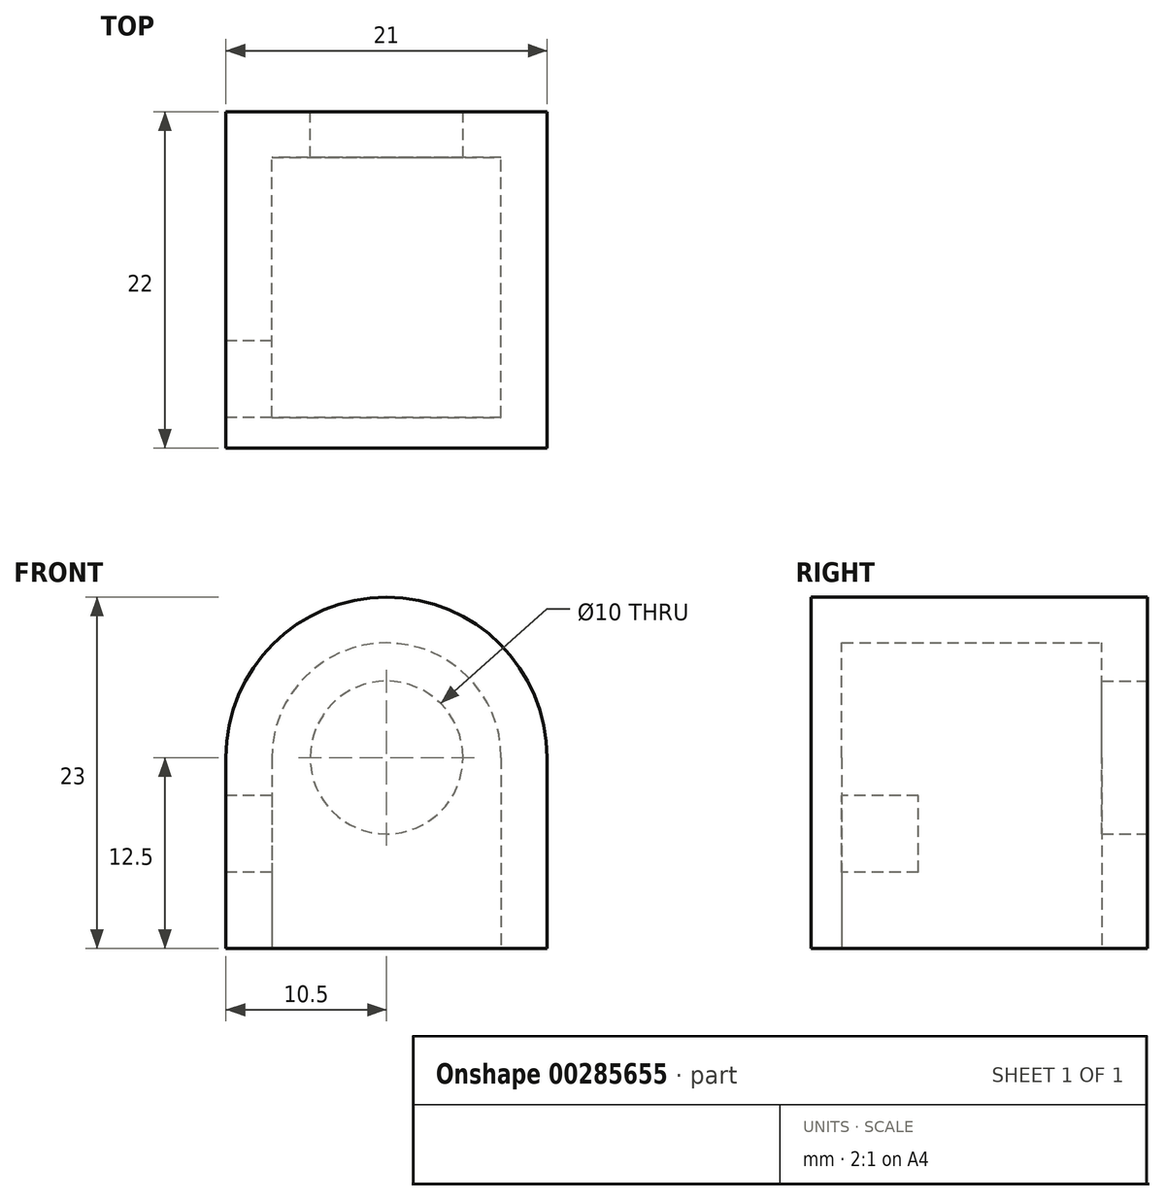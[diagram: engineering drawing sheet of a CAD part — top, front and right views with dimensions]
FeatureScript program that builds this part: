
annotation { "Feature Type Name" : "Feature", "Feature Type Description" : "" }
export const myFeature = defineFeature(function(context is Context, id is Id, definition is map)
    precondition{}
    {
        {
            var Q0;
            Q0=qCreatedBy(makeId("Front.planeOp"),FACE);
            var sketch = newSketch(context, id + "F0", { "sketchPlane" : qUnion([Q0])});
            skCircle(sketch, "E0", {"center": v(0, 0) * mm, "radius": 5 * mm});
            skArc(sketch, "E1", {"start": v(7.5, 0) * mm, "mid": v(0, 7.5) * mm, "end": v(-7.5, 0) * mm});
            skLineSegment(sketch, "E2.top", {"start": v(-7.5, -12.5) * mm, "end": v(7.5, -12.5) * mm});
            skLineSegment(sketch, "E2.left", {"start": v(-7.5, 0) * mm, "end": v(-7.5, -12.5) * mm});
            skLineSegment(sketch, "E2.right", {"start": v(7.5, 0) * mm, "end": v(7.5, -12.5) * mm});
            skSolve(sketch);
        }
        {
            var Q0;
            Q0=makeQuery(id+"F0.imprint","IMPRINT",FACE,{"disambiguationData":[TD([[makeQuery(id+"F0.imprint","IMPRINT",EDGE,{"derivedFrom":sQuery(id+"F0.wireOp",EDGE,"E0")}),-1.0]])]});
            extrude(context, id + "F1", {"entities" : qUnion([Q0]), "depth" : 3 * mm});
        }
        {
            var Q0;
            Q0=qCreatedBy(makeId("Front.planeOp"),FACE);
            var sketch = newSketch(context, id + "F2", { "sketchPlane" : qUnion([Q0])});
            skArc(sketch, "E3", {"start": v(10.5, 0) * mm, "mid": v(0, 10.5) * mm, "end": v(-10.5, 0) * mm});
            skLineSegment(sketch, "E4.top", {"start": v(-10.5, -12.5) * mm, "end": v(-7.5, -12.5) * mm});
            skLineSegment(sketch, "E4.left", {"start": v(-10.5, 0) * mm, "end": v(-10.5, -12.5) * mm});
            skLineSegment(sketch, "E4.right", {"start": v(10.5, 0) * mm, "end": v(10.5, -12.5) * mm});
            skArc(sketch, "E5", {"start": v(7.5, 0) * mm, "mid": v(0, 7.5) * mm, "end": v(-7.5, 0) * mm});
            skLineSegment(sketch, "E6", {"start": v(-7.5, 0) * mm, "end": v(-7.5, -12.5) * mm});
            skLineSegment(sketch, "E7", {"start": v(7.5, 0) * mm, "end": v(7.5, -12.5) * mm});
            skLineSegment(sketch, "E8", {"start": v(7.5, -12.5) * mm, "end": v(10.5, -12.5) * mm});
            skSolve(sketch);
        }
        {
            var Q0;
            Q0=makeQuery(id+"F2.imprint","IMPRINT",FACE,{"disambiguationData":[TD([[makeQuery(id+"F2.imprint","IMPRINT",EDGE,{"derivedFrom":sQuery(id+"F2.wireOp",EDGE,"E3")}),1.0]])]});
            extrude(context, id + "F3", {"entities" : qUnion([Q0]), "operationType" : NewBodyOperationType.ADD, "depth" : 20 * mm});
        }
        {
            var Q0;
            Q0=makeQuery(id+"F3.opExtrude","CAP_FACE",FACE,{"disambiguationData":[OSD([sQuery(id+"F2.wireOp",EDGE,"E3"),sQuery(id+"F2.wireOp",EDGE,"E4.top"),sQuery(id+"F2.wireOp",EDGE,"E4.left"),sQuery(id+"F2.wireOp",EDGE,"E4.right"),sQuery(id+"F2.wireOp",EDGE,"E5"),sQuery(id+"F2.wireOp",EDGE,"E6"),sQuery(id+"F2.wireOp",EDGE,"E7"),sQuery(id+"F2.wireOp",EDGE,"E8")])],"isStart":false});
            var sketch = newSketch(context, id + "F4", { "sketchPlane" : qUnion([Q0])});
            skArc(sketch, "E9", {"start": v(10.5, 0) * mm, "mid": v(0, 10.5) * mm, "end": v(-10.5, 0) * mm});
            skLineSegment(sketch, "E10", {"start": v(-10.5, 0) * mm, "end": v(-10.5, -12.5) * mm});
            skLineSegment(sketch, "E11", {"start": v(-10.5, -12.5) * mm, "end": v(10.5, -12.5) * mm});
            skLineSegment(sketch, "E12", {"start": v(10.5, -12.5) * mm, "end": v(10.5, 0) * mm});
            skSolve(sketch);
        }
        {
            var Q0;
            Q0=qSketchRegion(id+"F4",true);
            extrude(context, id + "F5", {"entities" : qUnion([Q0]), "operationType" : NewBodyOperationType.ADD, "depth" : 2 * mm});
        }
        {
            var Q0;
            Q0=makeQuery(id+"F5.boolean.opBoolean","MERGE",FACE,{"derivedFrom":[makeQuery(id+"F3.opExtrude","SWEPT_FACE",FACE,{"disambiguationData":[OSD([sQuery(id+"F2.wireOp",EDGE,"E4.left")])]}),makeQuery(id+"F5.opExtrude","SWEPT_FACE",FACE,{"disambiguationData":[OSD([sQuery(id+"F4.wireOp",EDGE,"E10")])]})]});
            var sketch = newSketch(context, id + "F6", { "sketchPlane" : qUnion([Q0])});
            skLineSegment(sketch, "E13.bottom", {"start": v(15, -7.5) * mm, "end": v(20, -7.5) * mm});
            skLineSegment(sketch, "E13.top", {"start": v(15, -2.5) * mm, "end": v(20, -2.5) * mm});
            skLineSegment(sketch, "E13.left", {"start": v(15, -7.5) * mm, "end": v(15, -2.5) * mm});
            skLineSegment(sketch, "E13.right", {"start": v(20, -7.5) * mm, "end": v(20, -2.5) * mm});
            skPoint(sketch, "E13.middle", {"position": v(17.5, -5) * mm});
            skSolve(sketch);
        }
        {
            var Q0;
            Q0=makeQuery(id+"F6.imprint","IMPRINT",FACE,{"disambiguationData":[TD([[makeQuery(id+"F6.imprint","IMPRINT",EDGE,{"derivedFrom":sQuery(id+"F6.wireOp",EDGE,"E13.bottom")}),1.0]])]});
            extrude(context, id + "F7", {"entities" : qUnion([Q0]), "operationType" : NewBodyOperationType.REMOVE, "oppositeDirection" : true, "depth" : 5 * mm, "offsetDistance" : 25 * mm});
        }
    });
